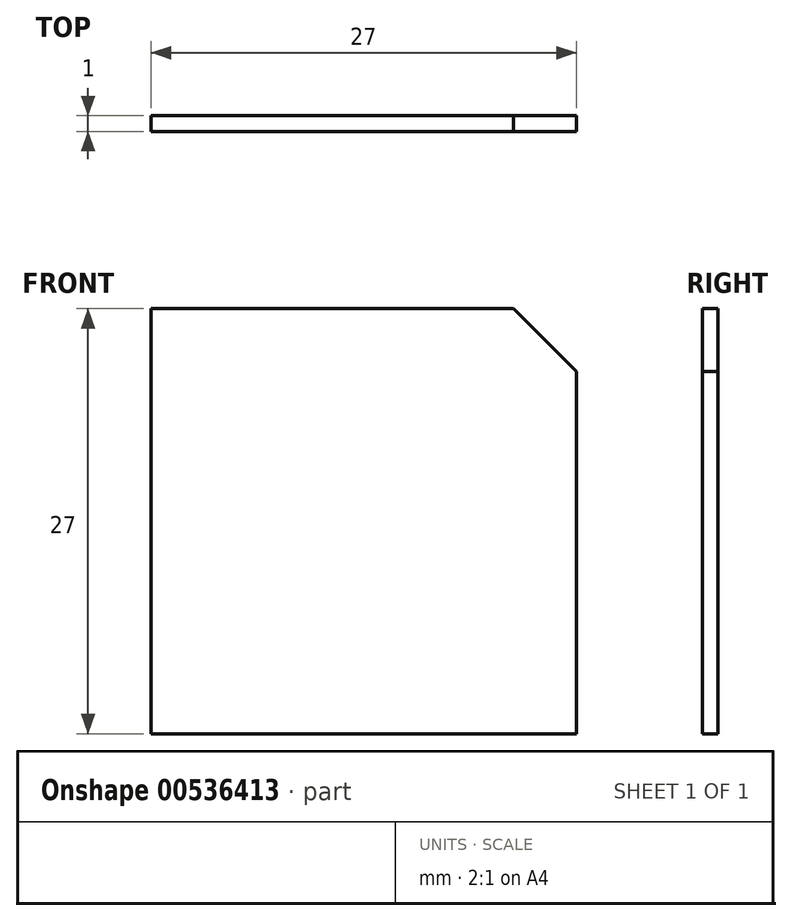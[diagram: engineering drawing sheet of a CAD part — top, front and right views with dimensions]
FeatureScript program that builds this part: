
annotation { "Feature Type Name" : "Feature", "Feature Type Description" : "" }
export const myFeature = defineFeature(function(context is Context, id is Id, definition is map)
    precondition{}
    {
        {
            var Q0;
            Q0=qCreatedBy(makeId("Front.planeOp"),FACE);
            var sketch = newSketch(context, id + "F0", { "sketchPlane" : qUnion([Q0])});
            skLineSegment(sketch, "E0", {"start": v(0, 27) * mm, "end": v(0, 0) * mm});
            skLineSegment(sketch, "E1", {"start": v(0, 0) * mm, "end": v(27, 0) * mm});
            skLineSegment(sketch, "E2", {"start": v(27, 0) * mm, "end": v(27, 23) * mm});
            skLineSegment(sketch, "E3", {"start": v(0, 27) * mm, "end": v(23.01, 27) * mm});
            skLineSegment(sketch, "E4", {"start": v(23.01, 27) * mm, "end": v(27, 23) * mm});
            skSolve(sketch);
        }
        {
            var Q0;
            Q0=qSketchRegion(id+"F0",true);
            extrude(context, id + "F1", {"entities" : qUnion([Q0]), "depth" : 1 * mm});
        }
    });
